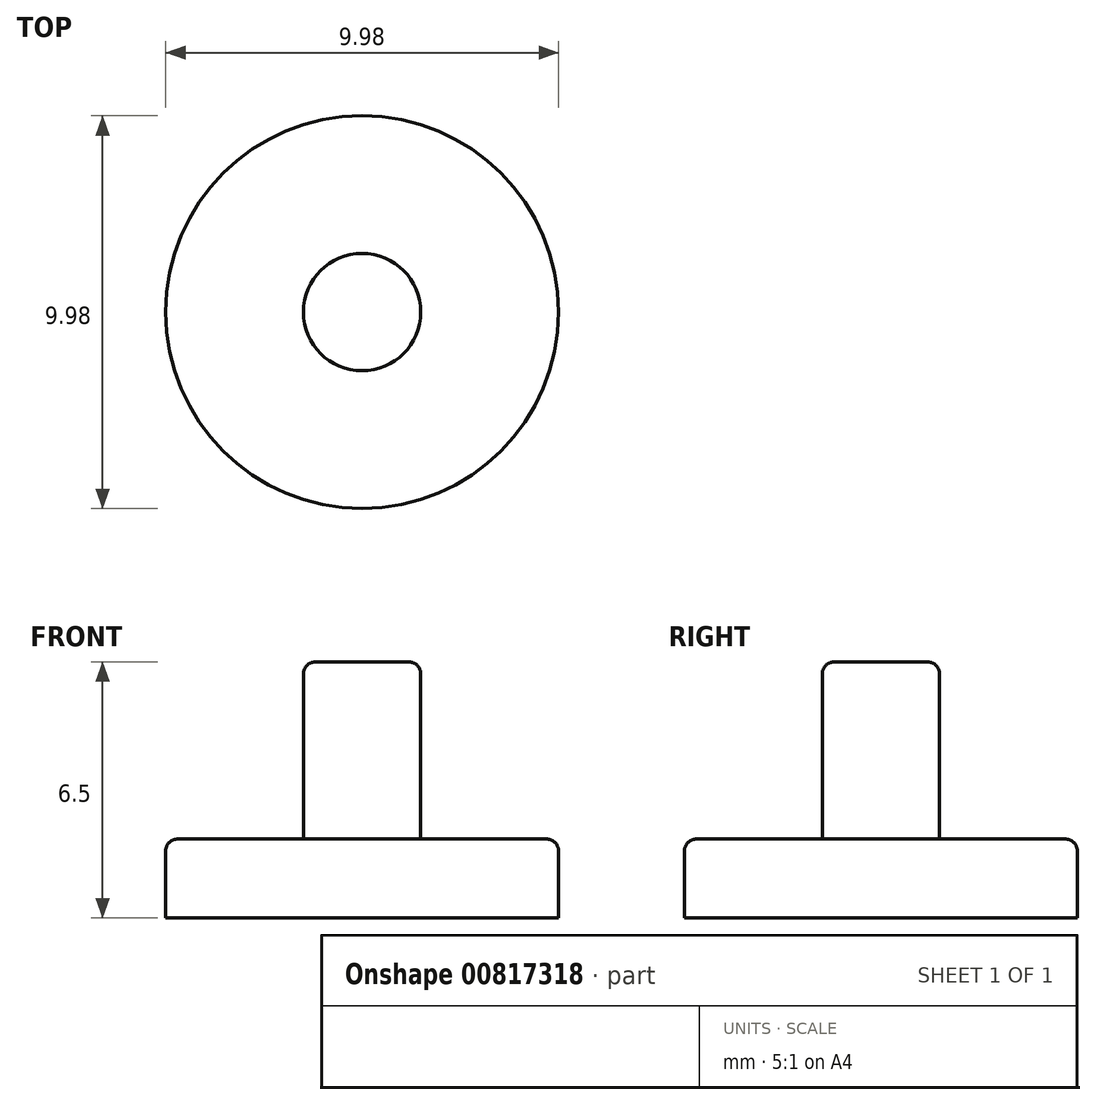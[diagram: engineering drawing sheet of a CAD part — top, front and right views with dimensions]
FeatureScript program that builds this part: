
annotation { "Feature Type Name" : "Feature", "Feature Type Description" : "" }
export const myFeature = defineFeature(function(context is Context, id is Id, definition is map)
    precondition{}
    {
        {
            var Q0;
            Q0=qCreatedBy(makeId("Top.planeOp"),FACE);
            var sketch = newSketch(context, id + "F0", { "sketchPlane" : qUnion([Q0])});
            skCircle(sketch, "E0", {"center": v(0, 0) * mm, "radius": 5 * mm});
            skSolve(sketch);
        }
        {
            var Q0;
            Q0=makeQuery(id+"F0.imprint","IMPRINT",FACE,{"disambiguationData":[TD([[makeQuery(id+"F0.imprint","IMPRINT",EDGE,{"derivedFrom":sQuery(id+"F0.wireOp",EDGE,"E0")}),1.0]])]});
            extrude(context, id + "F1", {"entities" : qUnion([Q0]), "depth" : 2 * mm, "offsetDistance" : 25 * mm});
        }
        {
            var Q0;
            Q0=makeQuery(id+"F1.opExtrude","CAP_FACE",FACE,{"disambiguationData":[OSD([sQuery(id+"F0.wireOp",EDGE,"E0")])],"isStart":false});
            var sketch = newSketch(context, id + "F2", { "sketchPlane" : qUnion([Q0])});
            skCircle(sketch, "E1", {"center": v(0, 0) * mm, "radius": 1.49 * mm});
            skSolve(sketch);
        }
        {
            var Q0;
            Q0 = qSketchRegion(id + "F2", true);
            extrude(context, id + "F3", {"entities" : qUnion([Q0]), "operationType" : NewBodyOperationType.ADD, "depth" : 4.5 * mm, "offsetDistance" : 25 * mm});
        }
        {
            var Q0;
            Q0=makeQuery(id+"F3.opExtrude","CAP_FACE",FACE,{"disambiguationData":[OSD([sQuery(id+"F2.wireOp",EDGE,"E1")])],"isStart":false});
            var Q1;
            Q1=makeQuery(id+"F1.opExtrude","CAP_EDGE",EDGE,{"disambiguationData":[OSD([sQuery(id+"F0.wireOp",EDGE,"E0")])],"isStart":false});
            fillet(context, id + "F4", {"entities" : qUnion([Q0, Q1]), "radius" : .3 * mm, "tangentPropagation" : true, "allowEdgeOverflow" : false});
        }
    });
